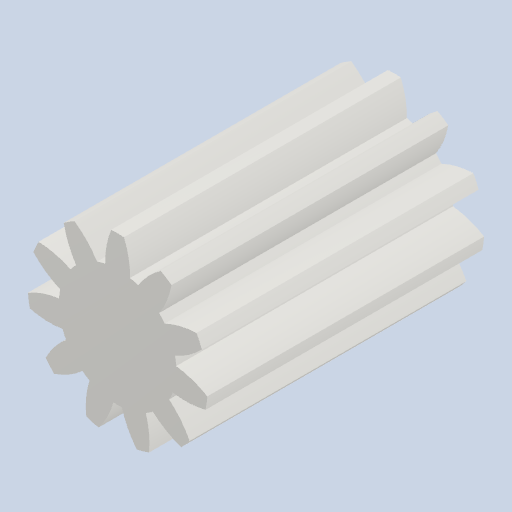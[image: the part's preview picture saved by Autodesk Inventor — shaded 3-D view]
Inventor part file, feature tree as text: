
AUTODESK INVENTOR PART (.ipt)
format: ipt  version: 2022 (Build 260153000, 153)  size: 199,680 bytes
history: native  units: mm (DEFAULTED — no unit token found)
features: plane x3, other x3, sketch x2, extrude x1
ambient origin geometry x8: Origin, YZ Plane, XZ Plane, XY Plane, X Axis, Y Axis, Z Axis, Center Point
bodies: Solid1 (feature_tree)
feature tree (9):
  extrude  "Extrusion1"  Depth=20.0mm TaperAngle=0.0deg
  plane  "Work Plane2"
  plane  "Work Plane8"
  plane  "Work Plane9"
  other  "Цилиндрическое зубчатое зацепление"
  sketch  "Sketch1"  dims[d0=13.0mm d1=20.0mm d2=0.0mm]
  sketch  "Sketch2"  dims[d3=11.0mm d4=10.0mm d5=0.0mm d16=19.5mm d17=0.0mm d34=2.855993mm d39=0.0mm d41=0.0mm d43=19.5mm d46=19.5mm d47=0.0mm d48=0.0mm]
  other  "Srf1"
  other  "Средний диаметр"
